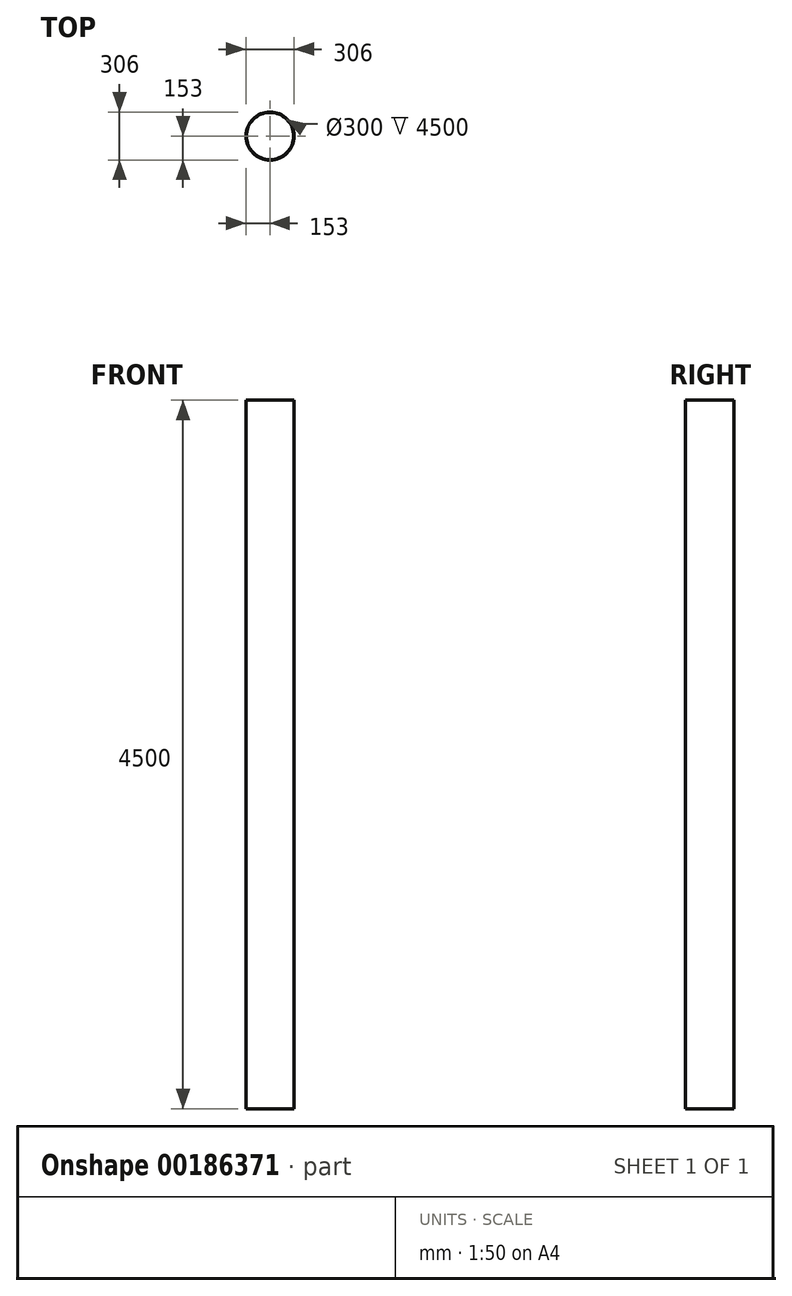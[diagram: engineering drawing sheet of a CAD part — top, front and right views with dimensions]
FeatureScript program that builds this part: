
annotation { "Feature Type Name" : "Feature", "Feature Type Description" : "" }
export const myFeature = defineFeature(function(context is Context, id is Id, definition is map)
    precondition{}
    {
        {
            var Q0;
            Q0=qCreatedBy(makeId("Top.planeOp"),FACE);
            var sketch = newSketch(context, id + "F0", { "sketchPlane" : qUnion([Q0])});
            skCircle(sketch, "E0", {"center": v(0, 0) * mm, "radius": 153 * mm});
            skCircle(sketch, "E1", {"center": v(0, 0) * mm, "radius": 150 * mm});
            skSolve(sketch);
        }
        {
            var Q0;
            Q0 = qSketchRegion(id + "F0", true);
            extrude(context, id + "F1", {"entities" : qUnion([Q0]), "depth" : 4500 * mm});
        }
    });
